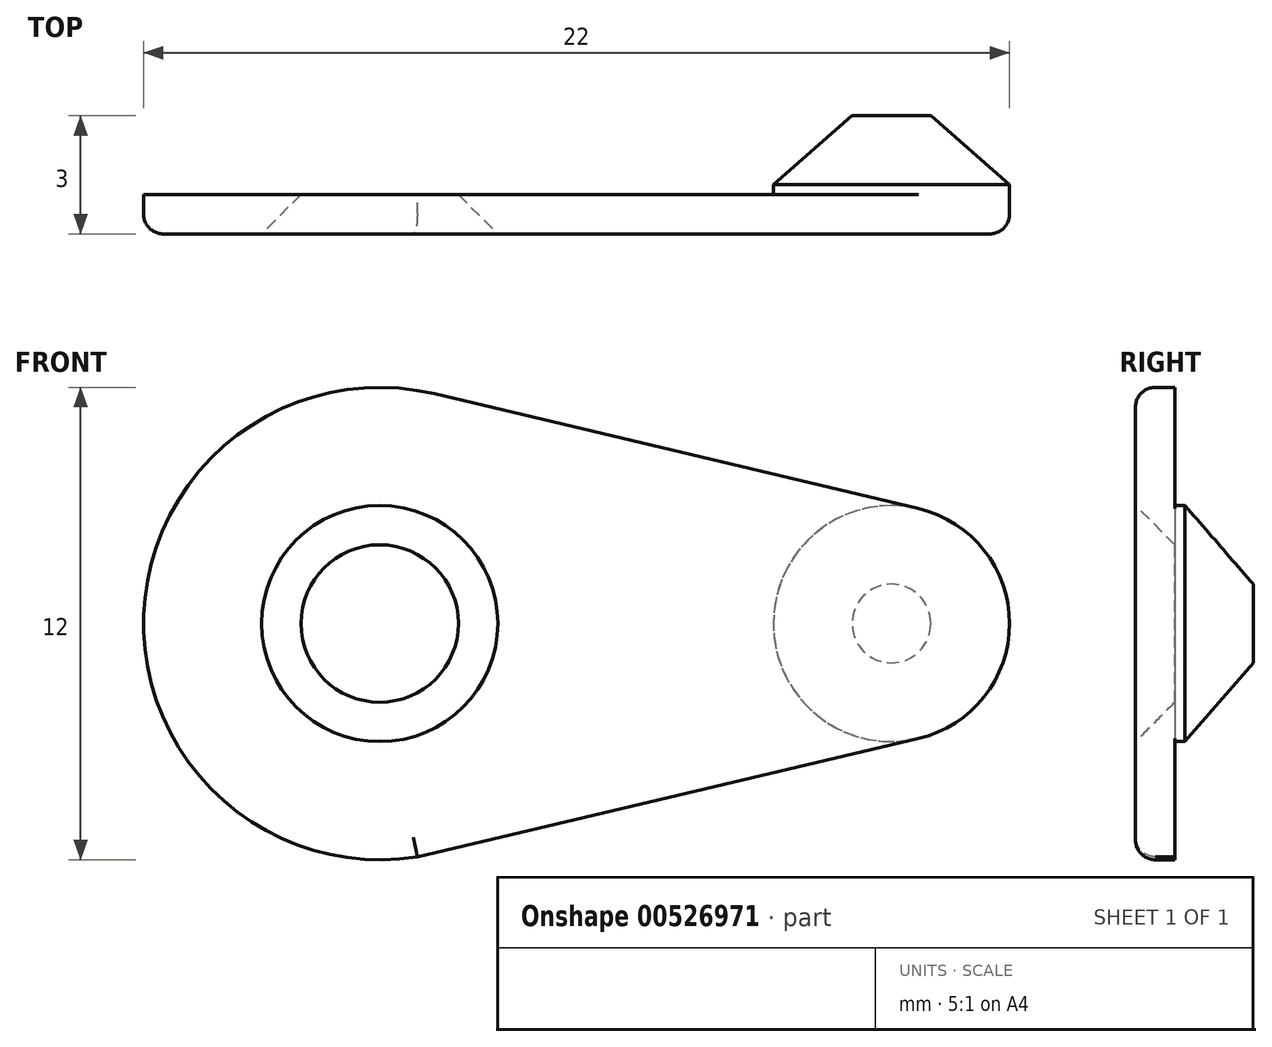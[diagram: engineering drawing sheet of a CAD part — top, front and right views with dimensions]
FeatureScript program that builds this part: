
annotation { "Feature Type Name" : "Feature", "Feature Type Description" : "" }
export const myFeature = defineFeature(function(context is Context, id is Id, definition is map)
    precondition{}
    {
        {
            var Q0;
            Q0=qCreatedBy(makeId("Front.planeOp"),FACE);
            var sketch = newSketch(context, id + "F0", { "sketchPlane" : qUnion([Q0])});
            skCircle(sketch, "E0", {"center": v(0, 0) * mm, "radius": 1.5 * mm});
            skArc(sketch, "E1", {"start": v(13, 3) * mm, "mid": v(16, 0) * mm, "end": v(13, -3) * mm});
            skLineSegment(sketch, "E2", {"start": v(19.5, 0) * mm, "end": v(-7.8, 0) * mm});
            skArc(sketch, "E3", {"start": v(0.96, -5.92) * mm, "mid": v(-6, 0.22) * mm, "end": v(1.38, 5.84) * mm});
            skLineSegment(sketch, "E4", {"start": v(1.38, 5.84) * mm, "end": v(13.7, 2.92) * mm});
            skLineSegment(sketch, "E5", {"start": v(0.96, -5.92) * mm, "end": v(13.69, -2.92) * mm});
            skSolve(sketch);
        }
        {
            var Q0;
            {var subQ1=sQuery(id+"F0.wireOp",EDGE,"E2");var subQ3=sQuery(id+"F0.wireOp",EDGE,"E0");var subQ7=makeQuery(id+"F0.imprint","INTERSECT",VERTEX,{"disambiguationData":[OD(0.0)],"derivedFrom":[subQ3,subQ1]});Q0=makeQuery(id+"F0.imprint","IMPRINT",FACE,{"disambiguationData":[TD([[makeQuery(id+"F0.imprint","IMPRINT",EDGE,{"disambiguationData":[TD([[subQ7,1.0]])],"derivedFrom":subQ3}),-1.0]])]});}
            var Q1;
            {var subQ3=sQuery(id+"F0.wireOp",EDGE,"E2");var subQ7=sQuery(id+"F0.wireOp",EDGE,"E0");var subQ8=makeQuery(id+"F0.imprint","INTERSECT",VERTEX,{"disambiguationData":[OD(0.0)],"derivedFrom":[subQ7,subQ3]});Q1=makeQuery(id+"F0.imprint","IMPRINT",FACE,{"disambiguationData":[TD([[makeQuery(id+"F0.imprint","IMPRINT",EDGE,{"disambiguationData":[TD([[subQ8,-1.0]])],"derivedFrom":subQ7}),-1.0]])]});}
            extrude(context, id + "F1", {"entities" : qUnion([Q0, Q1]), "depth" : 1 * mm, "offsetDistance" : 25 * mm});
        }
        {
            var Q0;
            Q0=makeQuery(id+"F1.opExtrude","CAP_FACE",FACE,{"disambiguationData":[OSD([sQuery(id+"F0.wireOp",EDGE,"E0"),sQuery(id+"F0.wireOp",EDGE,"4f7b179f-feef-4eca-b298-d81a723d1c31.top"),sQuery(id+"F0.wireOp",EDGE,"E1"),sQuery(id+"F0.wireOp",EDGE,"5SnvhKks-tK3v-3HMV-XfQK-MJqVifFDtKC4"),sQuery(id+"F0.wireOp",EDGE,"E3")])],"isStart":true});
            var sketch = newSketch(context, id + "F2", { "sketchPlane" : qUnion([Q0])});
            skCircle(sketch, "E6", {"center": v(-13, 0) * mm, "radius": 3 * mm});
            skSolve(sketch);
        }
        {
            var Q0;
            {var subQ0=sQuery(id+"F2.wireOp",EDGE,"E6");var subQ1=makeQuery(id+"F2.imprint","INTERSECT",VERTEX,{"derivedFrom":[makeQuery(id+"F1.opExtrude","CAP_EDGE",EDGE,{"disambiguationData":[OSD([sQuery(id+"F0.wireOp",EDGE,"E4")])],"isStart":true}),subQ0]});Q0=makeQuery(id+"F2.imprint","IMPRINT",FACE,{"disambiguationData":[TD([[makeQuery(id+"F2.imprint","IMPRINT",EDGE,{"disambiguationData":[TD([[subQ1,-1.0]])],"derivedFrom":subQ0}),1.0]])]});}
            extrude(context, id + "F3", {"entities" : qUnion([Q0]), "operationType" : NewBodyOperationType.ADD, "depth" : 2 * mm, "offsetDistance" : 25 * mm});
        }
        {
            var Q0;
            Q0=makeQuery(id+"F1.opExtrude","CAP_EDGE",EDGE,{"disambiguationData":[OSD([sQuery(id+"F0.wireOp",EDGE,"E3")])],"isStart":false});
            fillet(context, id + "F4", {"entities" : qUnion([Q0]), "radius" : .5 * mm, "tangentPropagation" : true, "allowEdgeOverflow" : false});
        }
        {
            var Q0;
            Q0=makeQuery(id+"F1.opExtrude","CAP_EDGE",EDGE,{"disambiguationData":[OSD([sQuery(id+"F0.wireOp",EDGE,"E0")])],"isStart":false});
            chamfer(context, id + "F5", {"entities" : qUnion([Q0]), "width" : 1.5 * mm, "tangentPropagation" : true});
        }
        {
            var Q0;
            Q0=makeQuery(id+"F3.opExtrude","CAP_EDGE",EDGE,{"disambiguationData":[OSD([sQuery(id+"F2.wireOp",EDGE,"E6")])],"isStart":false});
            chamfer(context, id + "F6", {"entities" : qUnion([Q0]), "chamferType" : ChamferType.TWO_OFFSETS, "width1" : 1.75 * mm, "oppositeDirection" : false, "width2" : 2 * mm, "tangentPropagation" : true});
        }
    });
